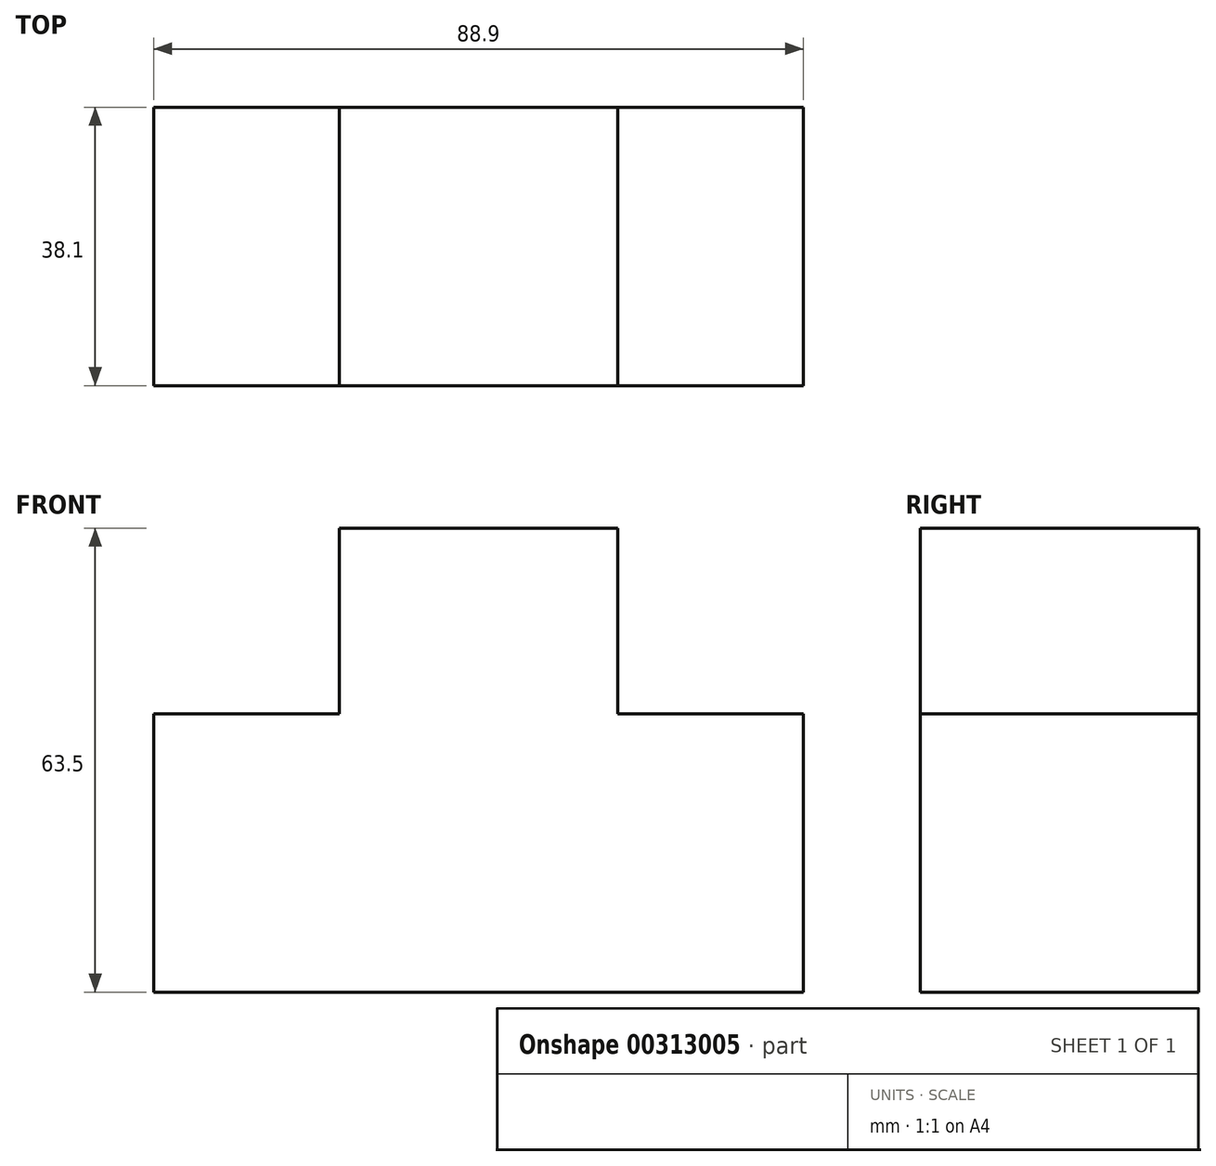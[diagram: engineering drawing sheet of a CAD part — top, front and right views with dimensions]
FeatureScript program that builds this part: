
annotation { "Feature Type Name" : "Feature", "Feature Type Description" : "" }
export const myFeature = defineFeature(function(context is Context, id is Id, definition is map)
    precondition{}
    {
        {
            var Q0;
            Q0=qCreatedBy(makeId("Front.planeOp"),FACE);
            var sketch = newSketch(context, id + "F0", { "sketchPlane" : qUnion([Q0])});
            skLineSegment(sketch, "E0", {"start": v(-35.25, -37.57) * mm, "end": v(53.65, -37.57) * mm});
            skLineSegment(sketch, "E1", {"start": v(53.65, -37.57) * mm, "end": v(53.65, 0.53) * mm});
            skLineSegment(sketch, "E2", {"start": v(53.65, 0.53) * mm, "end": v(28.25, 0.53) * mm});
            skLineSegment(sketch, "E3", {"start": v(28.25, 0.53) * mm, "end": v(28.25, 25.93) * mm});
            skLineSegment(sketch, "E4", {"start": v(28.25, 25.93) * mm, "end": v(-9.85, 25.93) * mm});
            skLineSegment(sketch, "E5", {"start": v(-9.85, 25.93) * mm, "end": v(-9.85, 0.53) * mm});
            skLineSegment(sketch, "E6", {"start": v(-9.85, 0.53) * mm, "end": v(-35.25, 0.53) * mm});
            skLineSegment(sketch, "E7", {"start": v(-35.25, 0.53) * mm, "end": v(-35.25, -37.57) * mm});
            skSolve(sketch);
        }
        {
            var Q0;
            Q0=makeQuery(id+"F0.imprint","IMPRINT",FACE,{"disambiguationData":[TD([[makeQuery(id+"F0.imprint","IMPRINT",EDGE,{"derivedFrom":sQuery(id+"F0.wireOp",EDGE,"E0")}),1.0]])]});
            extrude(context, id + "F1", {"entities" : qUnion([Q0]), "depth" : 38.1 * mm});
        }
    });
